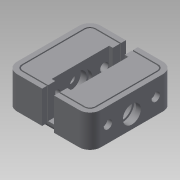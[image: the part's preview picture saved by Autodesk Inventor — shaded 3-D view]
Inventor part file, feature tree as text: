
AUTODESK INVENTOR PART (.ipt)
format: ipt  version: 2015 SP1 (Build 190203100, 203)  size: 329,728 bytes
history: native  units: mm
features: extrude x12, sketch x7, mirror x4, fillet x2, projected_geometry x2, plane x1
ambient origin geometry x8: Origin, YZ Plane, XZ Plane, XY Plane, X Axis, Y Axis, Z Axis, Center Point
bodies: Solid1 (feature_tree)
feature tree (28):
  sketch  "Sketch1"  dims[d0=30.0mm d1=30.0mm]
  extrude  "Extrusion1"  Depth=30.0mm
  extrude  "Extrusion2"  Depth=30.0mm TaperAngle=0.0deg
  extrude  "Extrusion3"  Depth=10.0mm
  sketch  "Sketch2"  dims[d2=3.0mm d3=0.0mm d4=30.0mm d5=0.0mm]
  extrude  "Extrusion6"  Depth=3.5mm
  extrude  "Extrusion7"  Depth=13.5mm TaperAngle=0.0deg
  extrude  "Extrusion8"  Depth=1.5mm
  extrude  "Extrusion9"  Depth=2.0mm
  fillet  "Fillet1"  Radius=2.0mm
  fillet  "Fillet2"  Radius=9.5mm
  plane  "Work Plane1"
  mirror  "Mirror3"
  mirror  "Mirror4"
  extrude  "Extrusion11"  Depth=0.5mm
  extrude  "Extrusion15"  Depth=0.5mm
  extrude  "Extrusion16"  Depth=2.0mm
  mirror  "Mirror7"
  extrude  "Extrusion17"  Depth=2.0mm
  extrude  "Extrusion18"  Depth=27.5mm TaperAngle=0.0deg
  mirror  "Mirror8"
  sketch  "Sketch6"  dims[d6=3.0mm d7=0.0mm d8=10.0mm]
  sketch  "Sketch10"  dims[d9=8.0mm d12=3.5mm]
  sketch  "Sketch11"  dims[d15=11.0mm d16=0.0mm d17=13.5mm d18=0.0mm]
  sketch  "Sketch12"  dims[d19=1.5mm d20=0.0mm d21=8.25mm]
  projected_geometry  "Projected Loop3"
  sketch  "Sketch13"  dims[d22=4.0mm d23=0.0mm d35=2.0mm d36=2.0mm d37=9.5mm d38=0.5mm d39=0.5mm d40=2.0mm d41=2.0mm d42=27.5mm d43=0.0mm d51=5.5mm d52=8.0mm d53=8.0mm d54=0.0mm d55=7.5mm d56=2.0mm d57=0.0mm d61=3.5mm d62=2.0mm d63=0.0mm d64=8.0mm d65=0.0mm d66=10.5mm]
  projected_geometry  "Projected Loop4"
